# Revit family: Windows_Purso_LK90eco_Single-Sash_Fixed-Window
name_source: partatom
category: Windows
revit_build: Autodesk Revit 2018 (Build: 20170223_1515(x64)
units: mm (PartAtom-declared; Revit-internal decimal feet)

## family parameters
Always vertical = Yes
Cut with Voids When Loaded = No
Host = Wall
OmniClass Number = 23.30.20.00
OmniClass Title = Windows
Room Calculation Point = No
Shared = No

## types (1)
- 1000mm x 1300mm
    Analytic Construction = <None>
    Assembly Code = B2020100
    Default Sill Height = 800 mm
    Description = Thermally highly insulated Window, fixed
    Edition number = 1
    Frame Material = Default
    Height = 1300 mm
    Keynote = 08500
    Manufacturer = Purso
    Model = LK90eco fixed window
    Product Guid = 9380d60f-9e04-48e6-8761-fb8f50c428d5
    Product data url = https://www.bimobject.com
    Type Comments = 1000mm x 1300mm
    URL = https://purso.fi
    Wall Closure = By host
    Width = 1000 mm  [stored 3.28084 ft]

note: [stored X ft] marks values corroborated as IEEE doubles in the binary element streams (Revit-internal decimal feet)

## geometry (parser evidence)
native form markers: Sweep x5
no freeform markers — native parametric forms only
